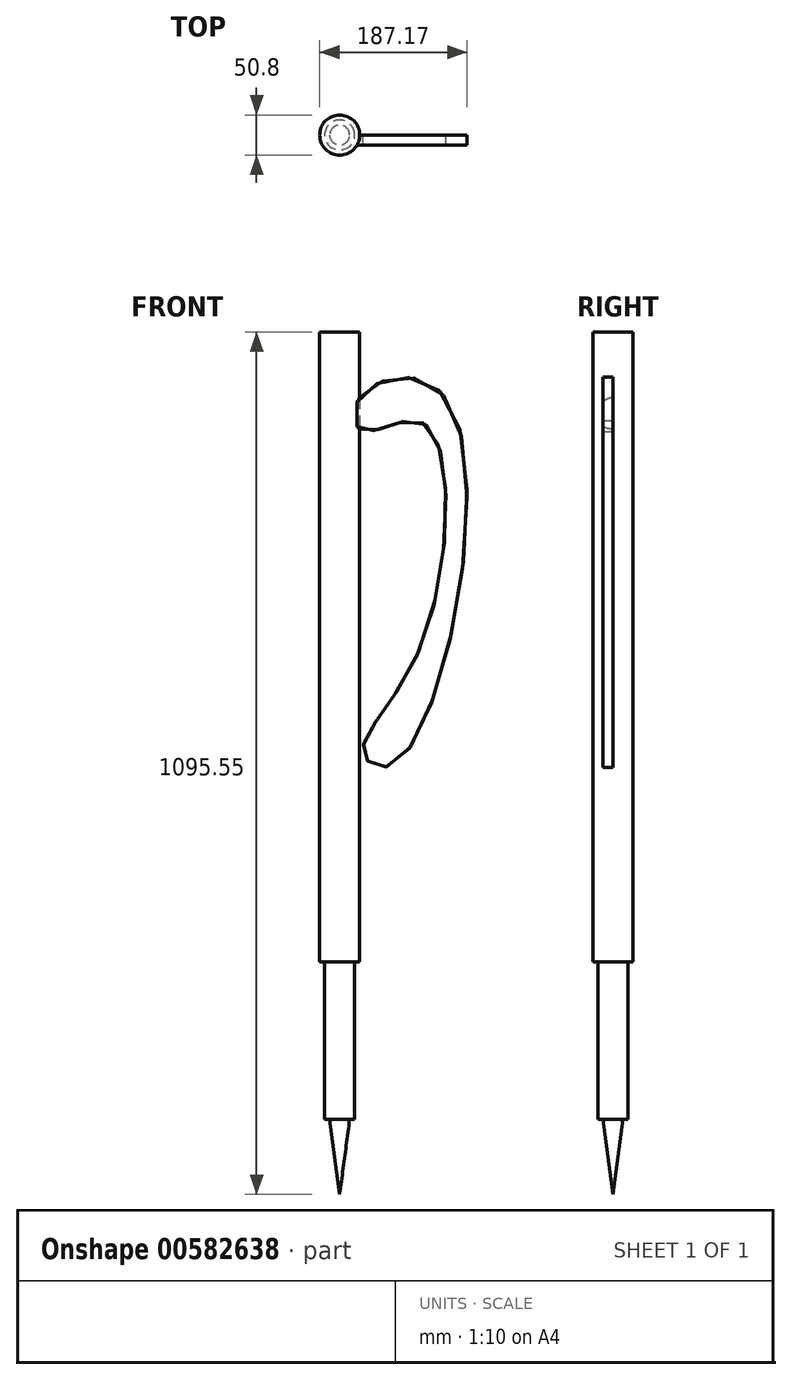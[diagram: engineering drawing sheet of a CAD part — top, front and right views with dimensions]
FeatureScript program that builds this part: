
annotation { "Feature Type Name" : "Feature", "Feature Type Description" : "" }
export const myFeature = defineFeature(function(context is Context, id is Id, definition is map)
    precondition{}
    {
        {
            var Q0;
            Q0=qCreatedBy(makeId("Front.planeOp"),FACE);
            var sketch = newSketch(context, id + "F0", { "sketchPlane" : qUnion([Q0])});
            skLineSegment(sketch, "E0", {"start": v(0, 0) * mm, "end": v(0, 355.6) * mm});
            skLineSegment(sketch, "E1", {"start": v(0, 355.6) * mm, "end": v(25.4, 355.6) * mm});
            skLineSegment(sketch, "E2", {"start": v(25.4, 355.6) * mm, "end": v(25.4, 0) * mm});
            skLineSegment(sketch, "E3", {"start": v(25.4, 0) * mm, "end": v(0, 0) * mm});
            skSolve(sketch);
        }
        {
            var Q0;
            Q0=qCreatedBy(makeId("Top.planeOp"),FACE);
            var sketch = newSketch(context, id + "F1", { "sketchPlane" : qUnion([Q0])});
            skCircle(sketch, "E4", {"center": v(0, 0) * mm, "radius": 25.4 * mm});
            skSolve(sketch);
        }
        {
            var Q0;
            Q0=makeQuery(id+"F1.imprint","IMPRINT",FACE,{"disambiguationData":[TD([[makeQuery(id+"F1.imprint","IMPRINT",EDGE,{"derivedFrom":sQuery(id+"F1.wireOp",EDGE,"E4")}),1.0]])]});
            extrude(context, id + "F2", {"entities" : qUnion([Q0]), "depth" : 800 * mm, "offsetDistance" : 25.4 * mm});
        }
        {
            var Q0;
            Q0=makeQuery(id+"F2.opExtrude","CAP_FACE",FACE,{"disambiguationData":[OSD([sQuery(id+"F1.wireOp",EDGE,"E4")])],"isStart":true});
            var sketch = newSketch(context, id + "F3", { "sketchPlane" : qUnion([Q0])});
            skCircle(sketch, "E5", {"center": v(0, 0) * mm, "radius": 19.05 * mm});
            skSolve(sketch);
        }
        {
            var Q0;
            Q0=makeQuery(id+"F3.imprint","IMPRINT",FACE,{"disambiguationData":[TD([[makeQuery(id+"F3.imprint","IMPRINT",EDGE,{"derivedFrom":sQuery(id+"F3.wireOp",EDGE,"E5")}),1.0]])]});
            extrude(context, id + "F4", {"entities" : qUnion([Q0]), "operationType" : NewBodyOperationType.ADD, "depth" : 200 * mm, "offsetDistance" : 25.4 * mm});
        }
        {
            var Q0;
            Q0=makeQuery(id+"F4.opExtrude","CAP_FACE",FACE,{"disambiguationData":[OSD([sQuery(id+"F3.wireOp",EDGE,"E5")])],"isStart":false});
            var sketch = newSketch(context, id + "F5", { "sketchPlane" : qUnion([Q0])});
            skCircle(sketch, "E6", {"center": v(0, 0) * mm, "radius": 12.7 * mm});
            skSolve(sketch);
        }
        {
            var Q0;
            Q0=qCreatedBy(makeId("Front.planeOp"),FACE);
            var sketch = newSketch(context, id + "F6", { "sketchPlane" : qUnion([Q0])});
            skCircle(sketch, "E7", {"center": v(0, -295.55) * mm, "radius": 12.7 * mm});
            skSolve(sketch);
        }
        {
            var Q1;
            Q1 = qSketchRegion(id + "F5", true);
            var Q2;
            Q2=sQuery(id+"F6.wireOp",VERTEX,"E7.center");
            loft(context, id + "F7", {"operationType" : NewBodyOperationType.ADD, "sheetProfilesArray" : [{ "sheetProfileEntities" : qUnion([Q1]) }, { "sheetProfileEntities" : qUnion([Q2]) }]});
        }
        {
            var Q0;
            Q0=qCreatedBy(makeId("Front.planeOp"),FACE);
            var sketch = newSketch(context, id + "F8", { "sketchPlane" : qUnion([Q0])});
            skFitSpline(sketch, "E8", {"points": [v(25.75, 717.43) * mm, v(135.65, 715.28) * mm, v(73.16, 254.11) * mm, v(30.06, 264.89) * mm, v(101.17, 396.34) * mm, v(105.48, 685.1) * mm, v(30.06, 674.33) * mm, v(25.75, 717.43) * mm]});
            skSolve(sketch);
        }
        {
            var Q0;
            Q0=makeQuery(id+"F8.imprint","IMPRINT",FACE,{"disambiguationData":[TD([[makeQuery(id+"F8.imprint","IMPRINT",EDGE,{"derivedFrom":sQuery(id+"F8.wireOp",EDGE,"E8")}),-1.0]])]});
            extrude(context, id + "F9", {"entities" : qUnion([Q0]), "operationType" : NewBodyOperationType.ADD, "depth" : 12.7 * mm, "offsetDistance" : 25.4 * mm});
        }
    });
